# Revit family: Gleiter radial-axial GL-100 o.Lasche, 1xAG
name_source: partatom
category: HLS-Bauteile
revit_build: Autodesk Revit 2017 (Build: 20190507_1515(x64)
units: mm (PartAtom-declared; Revit-internal decimal feet)

## family parameters
Arbeitsebenenbasiert = Ja
Beim Laden mit Abzugskörper schneiden = Nein
Bemaßung runder Anschluss = Durchmesser verwenden
Gemeinsam genutzt = Ja
Immer vertikal = Nein
Raumberechnungspunkt = Nein
Teiletyp = Normal

## types (4) — shared parameters
B1 = 36 mm  [stored 0.11811 ft]
Breite = 90 mm  [stored 0.295276 ft]
D0 = 14 mm  [stored 0.0459318 ft]
Fabrikat = MEFA
Gleitreibungsfaktor = 0.15 - 0.25
H1 = 11 mm  [stored 0.0360892 ft]
Haftreibungsfaktor = 0,2 - 0,3
Kurztext1 = Gleitelement radial-axial GL 100
L = 72 mm  [stored 0.23622 ft]
Länge = 160 mm  [stored 0.524934 ft]
Material Gleitstreifen = Kunststoff
Materialname Gleitstreifen = Polyamid 6
Mengeneinheit = St
Vorgabe-Ansicht = 1219 mm
max. Temperaturbeständigkeit = 100 °C
vpe = 1 St

## per-type parameters (varying)
| type | Artikelnummer | EAN | GL-100 | Gewicht | Gewicht pro Bauteil | H | H2 | Kurztext2 |
| Gleiter ra-ax GL-100, 1x M10 | 077048401 | 4250928417763 | Gleiter GL-100, 1xAG : Gleiter GL-100, AG M10 | 0.67 kg | 0.67 kg | 42 mm  [stored 0.137795 ft] | 53 mm | Anschluss 1 x M10 ohne Lasche |
| Gleiter ra-ax GL-100, 1x M12 | 077048301 | 4250928417749 | Gleiter GL-100, 1xAG : Gleiter GL-100, AG M12 | 0.68 kg | 0.68 kg | 44 mm  [stored 0.144357 ft] | 55 mm  [stored 0.180446 ft] | Anschluss 1 x M12 ohne Lasche |
| Gleiter ra-ax GL-100, 1x M16 | 077048501 | 4250928417787 | Gleiter GL-100, 1xAG : Gleiter GL-100, AG M16 | 0.69 kg | 0.69 kg | 43 mm  [stored 0.141076 ft] | 54 mm | Anschluss 1 x M16 ohne Lasche |
| Gleiter ra-ax GL-100, 1x 1/2" | 077048601 | 4250928417800 | Gleiter GL-100, 1xAG : Gleiter GL-100, AG Muffe halb Zoll | 0.68 kg | 0.68 kg | 43 mm  [stored 0.141076 ft] | 54 mm | Anschluss 1 x 1/2'' ohne Lasche |

note: [stored X ft] marks values corroborated as IEEE doubles in the binary element streams (Revit-internal decimal feet)

## geometry (parser evidence)
native form markers: Sweep x5
no freeform markers — native parametric forms only
